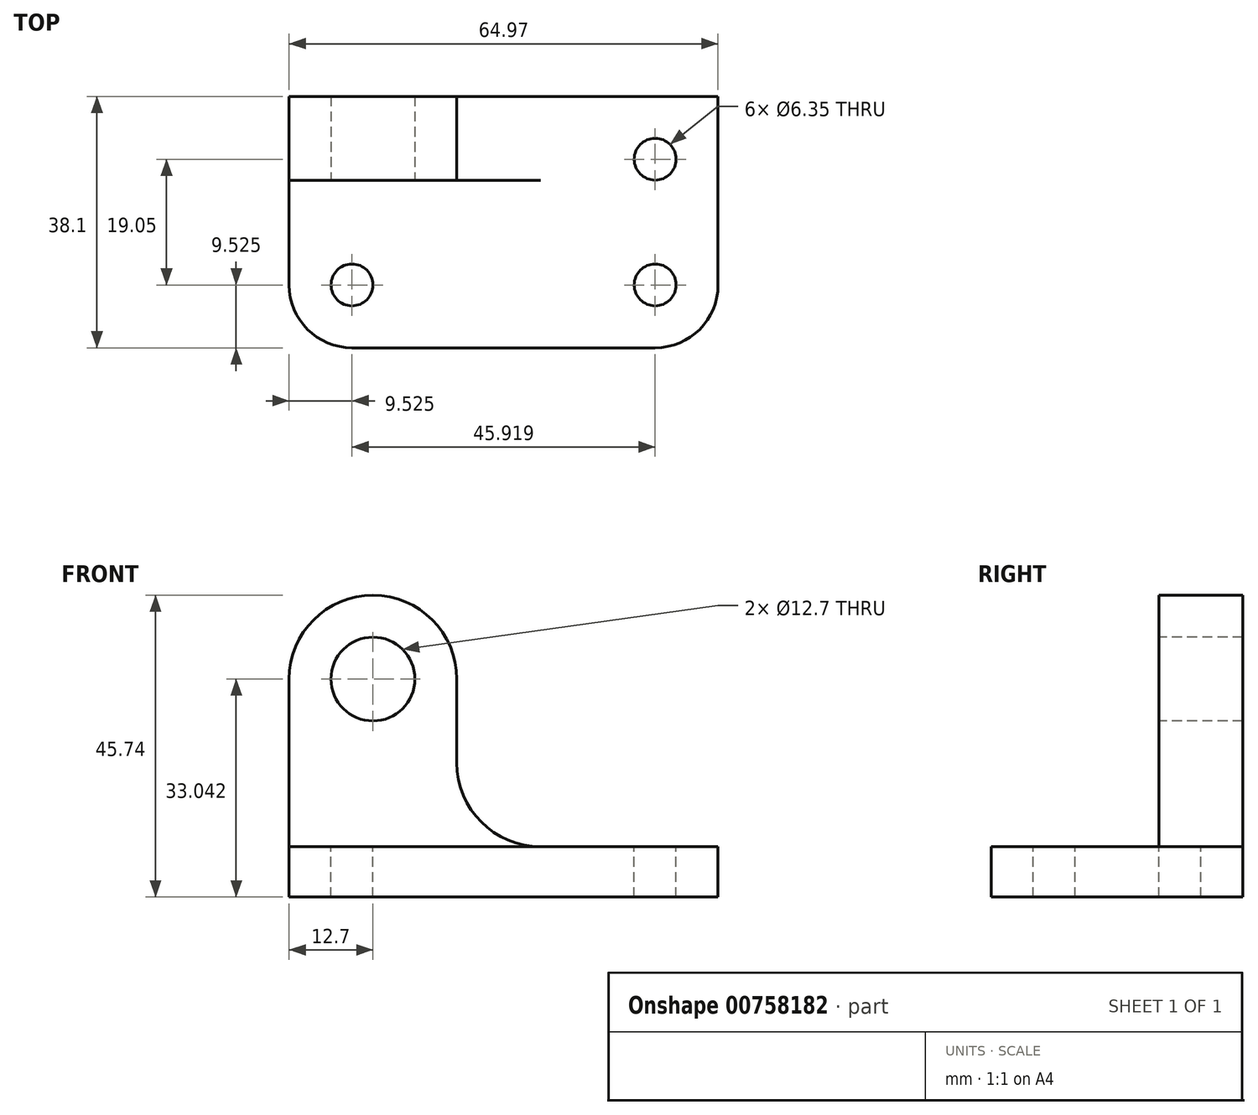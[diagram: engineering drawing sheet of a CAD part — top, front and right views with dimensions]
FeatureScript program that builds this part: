
annotation { "Feature Type Name" : "Feature", "Feature Type Description" : "" }
export const myFeature = defineFeature(function(context is Context, id is Id, definition is map)
    precondition{}
    {
        {
            var Q0;
            Q0=qCreatedBy(makeId("Front.planeOp"),FACE);
            var sketch = newSketch(context, id + "F0", { "sketchPlane" : qUnion([Q0])});
            skLineSegment(sketch, "E0", {"start": v(0, 0) * mm, "end": v(0, 45.74) * mm});
            skLineSegment(sketch, "E1", {"start": v(0, 45.74) * mm, "end": v(64.97, 45.74) * mm});
            skLineSegment(sketch, "E2", {"start": v(64.97, 45.74) * mm, "end": v(64.97, 0) * mm});
            skLineSegment(sketch, "E3", {"start": v(64.97, 0) * mm, "end": v(0, 0) * mm});
            skSolve(sketch);
        }
        {
            var Q0;
            Q0 = qSketchRegion(id + "F0", true);
            extrude(context, id + "F1", {"entities" : qUnion([Q0]), "oppositeDirection" : true, "depth" : 38.1 * mm, "offsetDistance" : 25.4 * mm});
        }
        {
            var Q0;
            Q0=makeQuery(id+"F1.opExtrude","SWEPT_FACE",FACE,{"disambiguationData":[OSD([sQuery(id+"F0.wireOp",EDGE,"E1")])]});
            var sketch = newSketch(context, id + "F2", { "sketchPlane" : qUnion([Q0])});
            skLineSegment(sketch, "E4", {"start": v(0, 25.4) * mm, "end": v(38.1, 25.4) * mm});
            skLineSegment(sketch, "E5", {"start": v(38.1, 25.4) * mm, "end": v(38.1, 38.1) * mm});
            skSolve(sketch);
        }
        {
            var Q0;
            Q0 = qSketchRegion(id + "F2", true);
            var Q1;
            {var subQ4=sQuery(id+"F2.wireOp",EDGE,"E4");Q1=makeQuery(id+"F2.imprint","IMPRINT",FACE,{"disambiguationData":[TD([[makeQuery(id+"F2.imprint","IMPRINT",EDGE,{"derivedFrom":subQ4}),-1.0]])]});}
            extrude(context, id + "F3", {"entities" : qUnion([Q0, Q1]), "operationType" : NewBodyOperationType.REMOVE, "oppositeDirection" : true, "depth" : 38.1 * mm, "offsetDistance" : 25.4 * mm});
        }
        {
            var Q0;
            Q0=makeQuery(id+"F3.boolean.opBoolean","COPY",FACE,{"derivedFrom":makeQuery(id+"F3.opExtrude","SWEPT_FACE",FACE,{"disambiguationData":[OSD([sQuery(id+"F2.wireOp",EDGE,"E4")])]})});
            var sketch = newSketch(context, id + "F4", { "sketchPlane" : qUnion([Q0])});
            skCircle(sketch, "E6", {"center": v(12.7, 33.04) * mm, "radius": 6.35 * mm});
            skArc(sketch, "E7", {"start": v(25.4, 33.04) * mm, "mid": v(12.7, 45.74) * mm, "end": v(0, 33.04) * mm});
            skLineSegment(sketch, "E8", {"start": v(25.4, 33.04) * mm, "end": v(25.4, 7.64) * mm});
            skArc(sketch, "E9", {"start": v(25.4, 20.34) * mm, "mid": v(29.12, 11.36) * mm, "end": v(38.1, 7.64) * mm});
            skSolve(sketch);
        }
        {
            var Q0;
            Q0 = qSketchRegion(id + "F4", true);
            var Q1;
            {var subQ0=sQuery(id+"F4.wireOp",EDGE,"E9");Q1=makeQuery(id+"F4.imprint","IMPRINT",FACE,{"disambiguationData":[TD([[makeQuery(id+"F4.imprint","IMPRINT",EDGE,{"derivedFrom":subQ0}),1.0]])]});}
            var Q2;
            {var subQ0=sQuery(id+"F4.wireOp",EDGE,"E7");var subQ1=sQuery(id+"F2.wireOp",EDGE,"E4");var subQ4=makeQuery(id+"F3.boolean.opBoolean","COPY",EDGE,{"derivedFrom":makeQuery(id+"F3.opExtrude","CAP_EDGE",EDGE,{"disambiguationData":[OSD([subQ1])],"isStart":true})});var subQ5=makeQuery(id+"F4.imprint","INTERSECT",VERTEX,{"derivedFrom":[subQ4,subQ0]});Q2=makeQuery(id+"F4.imprint","IMPRINT",FACE,{"disambiguationData":[TD([[makeQuery(id+"F4.imprint","IMPRINT",EDGE,{"disambiguationData":[TD([[subQ5,-1.0]])],"derivedFrom":subQ0}),-1.0]])]});}
            extrude(context, id + "F5", {"entities" : qUnion([Q0, Q1, Q2]), "operationType" : NewBodyOperationType.REMOVE, "oppositeDirection" : true, "depth" : 25.4 * mm, "offsetDistance" : 25.4 * mm});
        }
        {
            var Q0;
            Q0=makeQuery(id+"F3.boolean.opBoolean","COPY",FACE,{"derivedFrom":makeQuery(id+"F3.opExtrude","CAP_FACE",FACE,{"disambiguationData":[OSD([sQuery(id+"F0.wireOp",EDGE,"E0"),sQuery(id+"F0.wireOp",EDGE,"E1"),sQuery(id+"F0.wireOp",EDGE,"E2"),sQuery(id+"F2.wireOp",EDGE,"E4"),sQuery(id+"F2.wireOp",EDGE,"E5")])],"isStart":false})});
            var sketch = newSketch(context, id + "F6", { "sketchPlane" : qUnion([Q0])});
            skCircle(sketch, "E10", {"center": v(9.53, 9.52) * mm, "radius": 3.18 * mm});
            skArc(sketch, "E11", {"start": v(0, 9.52) * mm, "mid": v(2.79, 2.79) * mm, "end": v(9.52, 0) * mm});
            skCircle(sketch, "E12", {"center": v(55.44, 9.52) * mm, "radius": 3.18 * mm});
            skArc(sketch, "E13", {"start": v(55.44, 0) * mm, "mid": v(62.18, 2.79) * mm, "end": v(64.97, 9.53) * mm});
            skCircle(sketch, "E14", {"center": v(55.44, 28.58) * mm, "radius": 3.18 * mm});
            skSolve(sketch);
        }
        {
            var Q0;
            Q0 = qSketchRegion(id + "F6", true);
            var Q1;
            {var subQ0=sQuery(id+"F6.wireOp",EDGE,"E13");Q1=makeQuery(id+"F6.imprint","IMPRINT",FACE,{"disambiguationData":[TD([[makeQuery(id+"F6.imprint","IMPRINT",EDGE,{"derivedFrom":subQ0}),-1.0]])]});}
            var Q2;
            {var subQ0=sQuery(id+"F6.wireOp",EDGE,"E11");Q2=makeQuery(id+"F6.imprint","IMPRINT",FACE,{"disambiguationData":[TD([[makeQuery(id+"F6.imprint","IMPRINT",EDGE,{"derivedFrom":subQ0}),-1.0]])]});}
            extrude(context, id + "F7", {"entities" : qUnion([Q0, Q1, Q2]), "operationType" : NewBodyOperationType.REMOVE, "oppositeDirection" : true, "depth" : 25.4 * mm, "offsetDistance" : 25.4 * mm});
        }
    });
